# Revit family: Камин
name_source: partatom
category: Оборудование
units: mm (PartAtom-declared; Revit-internal decimal feet)

## family parameters
Всегда вертикально = Да
Классификация = Нет
На основе рабочей плоскости = Нет
Общий = Нет
При загрузке вырезать с полостями = Нет
Размер круглого соединителя = Использовать диаметр
Тип детали = Нормальный
Точка расчета площади = Нет

## types (12) — shared parameters
ADSK_Версия Revit = 2019
ADSK_Единица измерения = шт.
ADSK_Завод-изготовитель = Dimplex
ADSK_Классификация нагрузок = Прочее
ADSK_Код изделия = нет данных
ADSK_Количество = 1
ADSK_Количество фаз = 1
ADSK_Материал = Сталь, окрашенная, темно-серая, матовая
ADSK_Наименование краткое = Электрический очаг
ADSK_Напряжение = 230 В
ADSK_Номинальная мощность = 0 Вт
ADSK_Полная мощность = 0 В·А
ADSK_Ток = 0 А
B = 307 мм
H = 666 мм
b1 = 172 мм
b2 = 90 мм
h2 = 120 мм
h3 = 350 мм
Изображение типоразмера = <Нет>
zero-valued in all types: ADSK_Коэффициент мощности, ADSK_Масса

## per-type parameters (varying)
| type | ADSK_Наименование | L | L_потолка | Габариты | Длина_верхней_планки | Длина_нижней_планки | Длина_переднего_стекла | Левая заглушка | Левая_рамка_стекла | Левое_стекло | Левые планки | Наполнение камина 1000 | Наполнение камина 1500 | Наполнение камина 750 | Правая заглушка | Правая_рамка_стекла | Правое_стекло | Правые планки |
| Dimplex Vivente 75 | Очаг Vivente 75 | 750 мм | 730 мм | 665х788х321 | 750 мм | 750 мм | 750 мм | Нет | Да | Да | Да | Нет | Нет | Да | Нет | Да | Да | Да |
| Dimplex Vivente 100 | Очаг Vivente 100 | 1000 мм | 980 мм | 665х1040х321 | 1000 мм | 1000 мм | 1000 мм | Нет | Да | Да | Да | Да | Нет | Нет | Нет | Да | Да | Да |
| Dimplex Vivente 150 | Очаг Vivente 150 | 1500 мм | 1480 мм | 665х1538х321 | 1500 мм | 1500 мм | 1500 мм | Нет | Да | Да | Да | Нет | Да | Нет | Нет | Да | Да | Да |
| Dimplex Vivente 75 установка слева | Очаг Vivente 75 | 750 мм | 730 мм | 665х788х321 | 750 мм | 750 мм | 750 мм | Да | Нет | Нет | Нет | Нет | Нет | Да | Нет | Да | Да | Да |
| Dimplex Vivente 75 установка справа | Очаг Vivente 75 | 750 мм | 730 мм | 665х788х321 | 750 мм | 750 мм | 750 мм | Нет | Да | Да | Да | Нет | Нет | Да | Да | Нет | Нет | Нет |
| Dimplex Vivente 100 установка справа | Очаг Vivente 100 | 1000 мм | 980 мм | 665х1040х321 | 1000 мм | 1000 мм | 1000 мм | Нет | Да | Да | Да | Да | Нет | Нет | Да | Нет | Нет | Нет |
| Dimplex Vivente 100 установка слева | Очаг Vivente 100 | 1000 мм | 980 мм | 665х1040х321 | 1000 мм | 1000 мм | 1000 мм | Да | Нет | Нет | Нет | Да | Нет | Нет | Нет | Да | Да | Да |
| Dimplex Vivente 150 установка слева | Очаг Vivente 150 | 1500 мм | 1480 мм | 665х1538х321 | 1500 мм | 1500 мм | 1500 мм | Да | Нет | Нет | Нет | Нет | Да | Нет | Нет | Да | Да | Да |
| Dimplex Vivente 150 установка справа | Очаг Vivente 150 | 1500 мм | 1480 мм | 665х1538х321 | 1500 мм | 1500 мм | 1500 мм | Нет | Да | Да | Да | Нет | Да | Нет | Да | Нет | Нет | Нет |
| Dimplex Vivente 75 установка в нишу | Очаг Vivente 75 | 750 мм | 730 мм | 665х788х321 | 750 мм | 750 мм | 750 мм | Да | Нет | Нет | Нет | Нет | Нет | Да | Да | Нет | Нет | Нет |
| Dimplex Vivente 100 установка в нишу | Очаг Vivente 100 | 1000 мм | 980 мм | 665х1040х321 | 1000 мм | 1000 мм | 1000 мм | Да | Нет | Нет | Нет | Да | Нет | Нет | Да | Нет | Нет | Нет |
| Dimplex Vivente 150 установка в нишу | Очаг Vivente 150 | 1500 мм | 1480 мм | 665х1538х321 | 1500 мм | 1500 мм | 1500 мм | Да | Нет | Нет | Нет | Нет | Да | Нет | Да | Нет | Нет | Нет |
